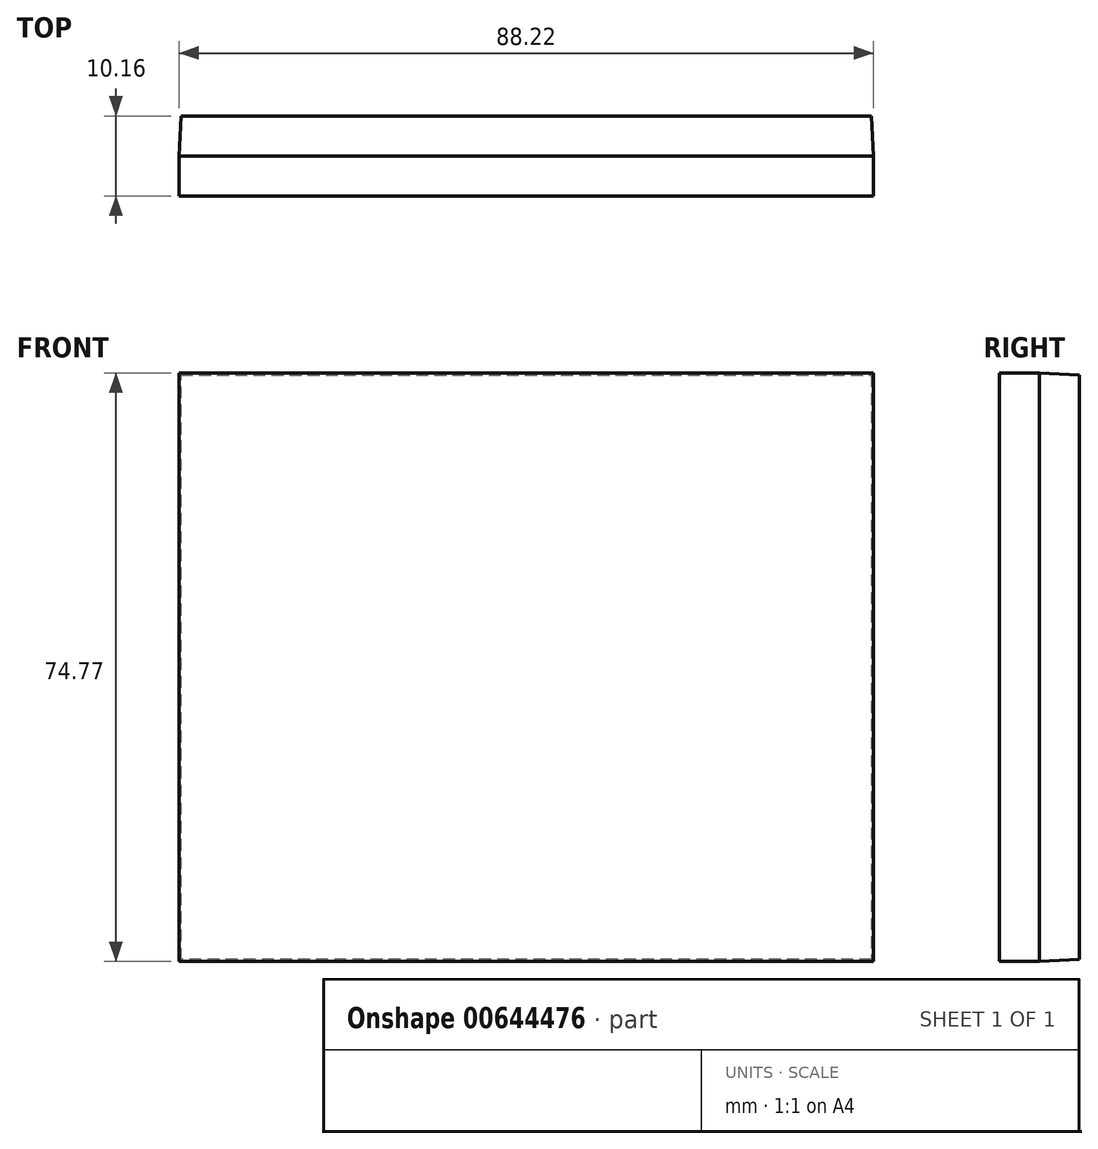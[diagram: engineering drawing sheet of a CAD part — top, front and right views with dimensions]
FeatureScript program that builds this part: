
annotation { "Feature Type Name" : "Feature", "Feature Type Description" : "" }
export const myFeature = defineFeature(function(context is Context, id is Id, definition is map)
    precondition{}
    {
        {
            var Q0;
            Q0=qCreatedBy(makeId("Front.planeOp"),FACE);
            var sketch = newSketch(context, id + "F0", { "sketchPlane" : qUnion([Q0])});
            skLineSegment(sketch, "E0.bottom", {"start": v(-42.68, 38.58) * mm, "end": v(45.54, 38.58) * mm});
            skLineSegment(sketch, "E0.top", {"start": v(-42.68, -36.2) * mm, "end": v(45.54, -36.2) * mm});
            skLineSegment(sketch, "E0.left", {"start": v(-42.68, 38.58) * mm, "end": v(-42.68, -36.2) * mm});
            skLineSegment(sketch, "E0.right", {"start": v(45.54, 38.58) * mm, "end": v(45.54, -36.2) * mm});
            skSolve(sketch);
        }
        {
            var Q0;
            Q0=makeQuery(id+"F0.imprint","IMPRINT",FACE,{"disambiguationData":[TD([[makeQuery(id+"F0.imprint","IMPRINT",EDGE,{"derivedFrom":sQuery(id+"F0.wireOp",EDGE,"E0.bottom")}),-1.0]])]});
            extrude(context, id + "F1", {"entities" : qUnion([Q0]), "depth" : 5.08 * mm, "offsetDistance" : 25.4 * mm, "hasSecondDirection" : true, "secondDirectionOppositeDirection" : true, "secondDirectionDepth" : 5.08 * mm, "hasSecondDirectionDraft" : true, "secondDirectionDraftAngle" : 3 * degree, "secondDirectionDraftPullDirection" : true});
        }
    });
